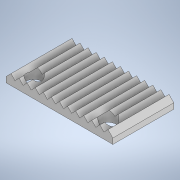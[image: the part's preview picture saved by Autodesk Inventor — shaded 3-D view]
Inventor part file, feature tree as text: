
AUTODESK INVENTOR PART (.ipt)
format: ipt  version: 2020 (Build 240168000, 168)  size: 210,432 bytes
history: native  units: in
note: dims shown in document units (in); Inventor stores cm internally (conversion verified against a paired STEP export)
features: extrude x4, sketch x4, mirror x1
ambient origin geometry x8: Origin, YZ Plane, XZ Plane, XY Plane, X Axis, Y Axis, Z Axis, Center Point
bodies: Solid1 (feature_tree)
feature tree (9):
  extrude  "Extrusion1"  Depth=0.6299in
  extrude  "Extrusion2"  Depth=0.5512in
  mirror  "Mirror1"
  extrude  "Extrusion3"  TaperAngle=135.0deg  [1 undecoded]
  extrude  "Extrusion4"  Depth=0.0591in TaperAngle=0.0deg
  sketch  "Sketch1"  dims[d0=1.1024in d1=0.6299in]
  sketch  "Sketch2"  dims[d2=0.1575in d3=0.0in d4=0.5512in]
  sketch  "Sketch3"  dims[d5=0.0591in d6=135.0deg]
  sketch  "Sketch4"  dims[d7=0.0591in d8=1.9685in d9=0.0in d10=0.1575in d11=0.1575in d12=1.9685in d13=0.0in d14=1.9685in d15=0.0in]
note: 1 required parameter value undecoded (feature->parameter linkage not recoverable at this tier; creation-order binding heuristic only, values carry confidence <= 0.55)
